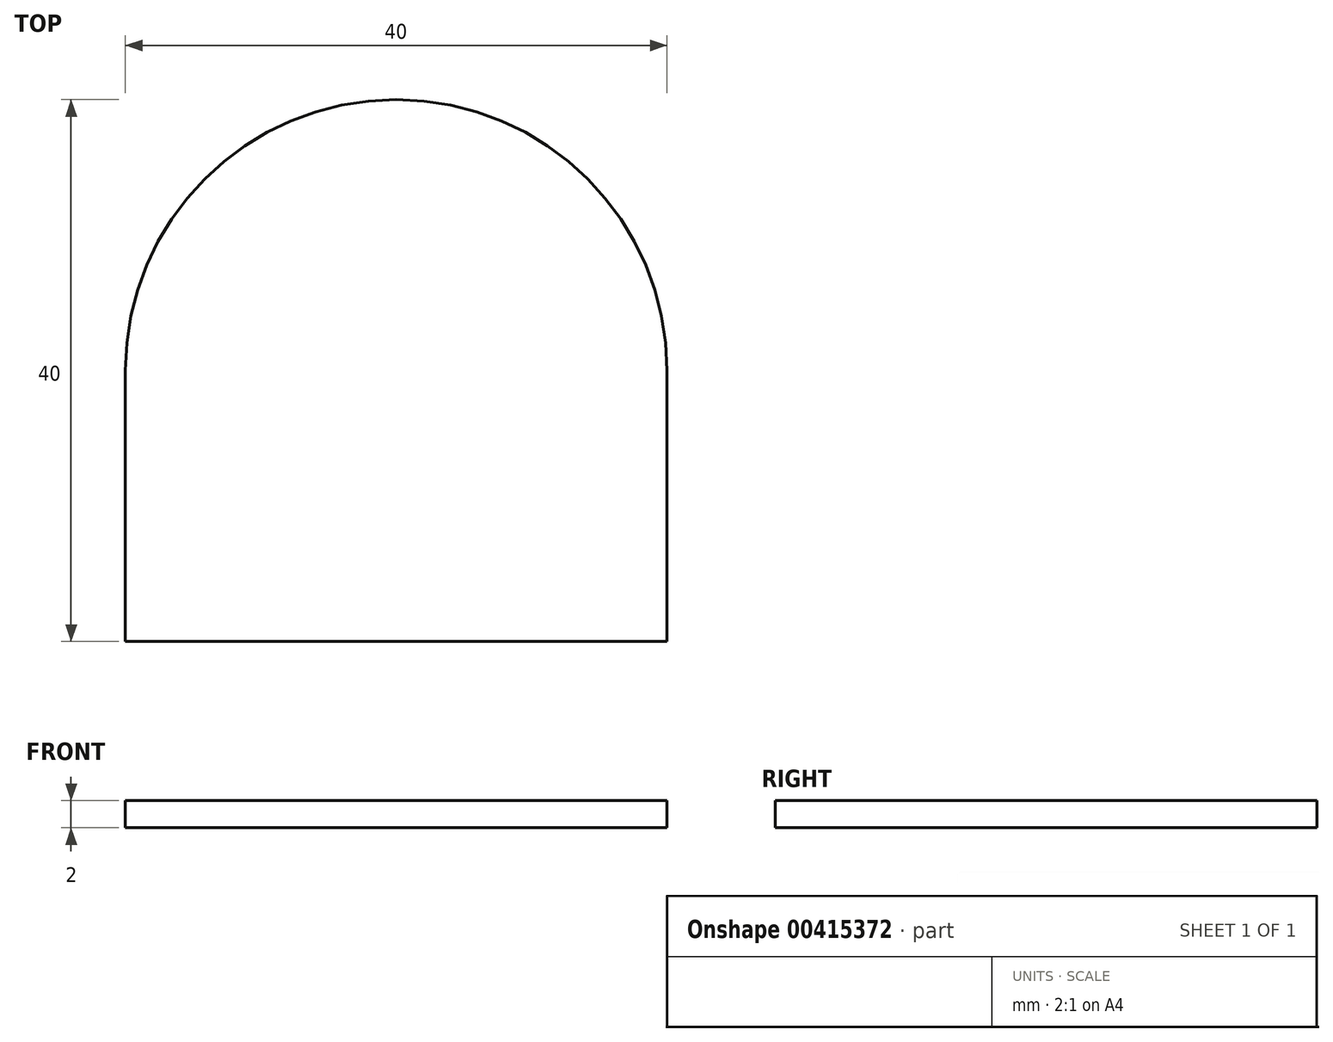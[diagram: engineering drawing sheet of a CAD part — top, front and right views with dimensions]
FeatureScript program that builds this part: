
annotation { "Feature Type Name" : "Feature", "Feature Type Description" : "" }
export const myFeature = defineFeature(function(context is Context, id is Id, definition is map)
    precondition{}
    {
        {
            var Q0;
            Q0=qCreatedBy(makeId("Top.planeOp"),FACE);
            var sketch = newSketch(context, id + "F0", { "sketchPlane" : qUnion([Q0])});
            skLineSegment(sketch, "E0.bottom", {"start": v(0, 0) * mm, "end": v(40, 0) * mm});
            skLineSegment(sketch, "E0.left", {"start": v(0, 0) * mm, "end": v(0, 20) * mm});
            skLineSegment(sketch, "E0.right", {"start": v(40, 0) * mm, "end": v(40, 20) * mm});
            skArc(sketch, "E1", {"start": v(40, 20) * mm, "mid": v(20, 40) * mm, "end": v(0, 20) * mm});
            skSolve(sketch);
        }
        {
            var Q0;
            Q0=makeQuery(id+"F0.imprint","IMPRINT",FACE,{"disambiguationData":[TD([[makeQuery(id+"F0.imprint","IMPRINT",EDGE,{"derivedFrom":sQuery(id+"F0.wireOp",EDGE,"E0.bottom")}),1.0]])]});
            extrude(context, id + "F1", {"entities" : qUnion([Q0]), "depth" : 2 * mm});
        }
    });
